# Revit family: M_Valve_Balancing and Control_MEPcontent_Oventrop_Hydrocontrol VFC 10626 DN 20-50 PN16 DIN
name_source: partatom
category: Pipe Accessories
revit_build: Autodesk Revit 2015 (Build: 20140223_1515(x64)
units: mm (PartAtom-declared; Revit-internal decimal feet)

## types (5) — shared parameters
Angle = 60.00°
Angle 2 = 30.00°
Angle 3 = -60.00°
Article Description = Double regulating and commissioning valve
Article Type = Hydrocontrol VFC 10626 DN 20-50 PN16 DIN
Black = Color RGB 35-35-35
Bronze = Color RGB 156-122-90
Content Supplier URL = www.mepcontent.eu
Custom = No
Description = Double regulating and commissioning valve
EMCS Version = 2.0
ETIM Article Class = EC011463
Family Version = 10.14
Hb5 = 3 mm  [stored 0.00984252 ft]
Hlp1 = 22 mm  [stored 0.0721785 ft]
IFCExportAs = IfcValveType
IFCExportType = PRESSUREREDUCING
Lgt1 = 2 mm  [stored 0.00656168 ft]
MEPcontent Class = VALVE_BALANCING
Manufacturer = Oventrop
Manufacturer URL = http://www.oventrop.de
Model = Hydrocontrol VFC 10626 DN 20-50 PN16 DIN
Pressure Drop = 0.0 Pa
Product Line = Oventrop
R1 = 9 mm  [stored 0.0295276 ft]
R2 = 10 mm  [stored 0.0328084 ft]
Revit Version = 2015
Steel = Color RGB 140-140-140
URL = www.stabiplan.com
r1 = 2 mm  [stored 0.00656168 ft]
r2 = 3 mm  [stored 0.00984252 ft]

## per-type parameters (varying)
- DN 40: CurDst=16 mm  [stored 0.0524934 ft]; Dst1=13 mm; FlangeDiameter=150 mm; GTIN=4026755126105; Hb1=140 mm; Hb2=51 mm; Hb6=53 mm; Height=136 mm; K=110 mm; L2=16 mm  [stored 0.0524934 ft]; Length=200 mm; Lgt2=15 mm  [stored 0.0492126 ft]; Lgt3=30 mm  [stored 0.0984252 ft]; Lgt4=87 mm; Manufacturer Art. No.=1062649; NominalDiameter=40 mm; OuterDiameter=48 mm  [stored 0.15748 ft]; Rad1=55 mm  [stored 0.180446 ft]; Rad2=75 mm; Rad3=31 mm; Rad4=28 mm; Rad5=30 mm  [stored 0.0984252 ft]; Rad6=33 mm  [stored 0.108268 ft]; Rad7=35 mm  [stored 0.114829 ft]; VDst=25 mm  [stored 0.082021 ft]; VHth=38 mm  [stored 0.124672 ft]
- DN 50: CurDst=19 mm  [stored 0.062336 ft]; Dst1=14 mm  [stored 0.0459318 ft]; FlangeDiameter=165 mm; GTIN=4026755126112; Hb1=150 mm; Hb2=58 mm; Hb6=61 mm; Height=145 mm; K=125 mm; L2=19 mm  [stored 0.062336 ft]; Length=230 mm; Lgt2=15 mm  [stored 0.0492126 ft]; Lgt3=37 mm; Lgt4=108 mm; Manufacturer Art. No.=1062650; NominalDiameter=50 mm; OuterDiameter=60 mm; Rad1=63 mm; Rad2=83 mm; Rad3=36 mm  [stored 0.11811 ft]; Rad4=33 mm  [stored 0.108268 ft]; Rad5=36 mm  [stored 0.11811 ft]; Rad6=38 mm  [stored 0.124672 ft]; Rad7=40 mm  [stored 0.131234 ft]; VDst=32 mm  [stored 0.104987 ft]; VHth=43 mm  [stored 0.141076 ft]
- DN 32: CurDst=13 mm; Dst1=7 mm  [stored 0.0229659 ft]; FlangeDiameter=140 mm; GTIN=4026755173215; Hb1=140 mm; Hb2=53 mm; Hb6=56 mm; Height=136 mm; K=100 mm; L2=13 mm; Length=180 mm; Lgt2=14 mm  [stored 0.0459318 ft]; Lgt3=24 mm  [stored 0.0787402 ft]; Lgt4=71 mm; Manufacturer Art. No.=1062648; NominalDiameter=32 mm; OuterDiameter=42 mm; Rad1=50 mm  [stored 0.164042 ft]; Rad2=70 mm; Rad3=26 mm; Rad4=23 mm; Rad5=26 mm; Rad6=28 mm; Rad7=30 mm  [stored 0.0984252 ft]; VDst=9 mm  [stored 0.0295276 ft]; VHth=71 mm
- DN 25: CurDst=11 mm  [stored 0.0360892 ft]; Dst1=14 mm  [stored 0.0459318 ft]; FlangeDiameter=115 mm; GTIN=4026755173178; Hb1=119 mm; Hb2=35 mm  [stored 0.114829 ft]; Hb6=34 mm; Height=118 mm; K=85 mm; L2=11 mm  [stored 0.0360892 ft]; Length=160 mm; Lgt2=14 mm  [stored 0.0459318 ft]; Lgt3=20 mm  [stored 0.0656168 ft]; Lgt4=69 mm; Manufacturer Art. No.=1062647; NominalDiameter=25 mm; OuterDiameter=34 mm; Rad1=43 mm  [stored 0.141076 ft]; Rad2=58 mm; Rad3=22 mm  [stored 0.0721785 ft]; Rad4=19 mm  [stored 0.062336 ft]; Rad5=22 mm  [stored 0.0721785 ft]; Rad6=24 mm  [stored 0.0787402 ft]; Rad7=26 mm; VDst=9 mm  [stored 0.0295276 ft]; VHth=51 mm
- DN 20: CurDst=10 mm  [stored 0.0328084 ft]; Dst1=10 mm  [stored 0.0328084 ft]; FlangeDiameter=105 mm; GTIN=4026755173154; Hb1=119 mm; Hb2=37 mm; Hb6=36 mm  [stored 0.11811 ft]; Height=118 mm; K=75 mm; L2=10 mm  [stored 0.0328084 ft]; Length=150 mm; Lgt2=14 mm  [stored 0.0459318 ft]; Lgt3=16 mm  [stored 0.0524934 ft]; Lgt4=61 mm; Manufacturer Art. No.=1062646; NominalDiameter=20 mm; OuterDiameter=27 mm; Rad1=38 mm  [stored 0.124672 ft]; Rad2=53 mm; Rad3=20 mm  [stored 0.0656168 ft]; Rad4=17 mm  [stored 0.0557743 ft]; Rad5=19 mm  [stored 0.062336 ft]; Rad6=22 mm  [stored 0.0721785 ft]; Rad7=24 mm  [stored 0.0787402 ft]; VDst=9 mm  [stored 0.0295276 ft]; VHth=49 mm

note: [stored X ft] marks values corroborated as IEEE doubles in the binary element streams (Revit-internal decimal feet)

## geometry (parser evidence)
native form markers: Blend x2, Sweep x2
no freeform markers — native parametric forms only
